# Revit family: 26891XXX_NEW
name_source: partatom
category: Plumbing Fixtures
revit_build: Autodesk Revit 2018 (Build: 20170223_1515(x64)
units: mm (PartAtom-declared; Revit-internal decimal feet)

## family parameters
Always vertical = No
Cut with Voids When Loaded = No
OmniClass Number = 23.45.00.00
OmniClass Title = Sanitary, Laundry, and Cleaning Equipment
Part Type = Normal
Room Calculation Point = No
Round Connector Dimension = Use Diameter
Shared = No
Work Plane-Based = Yes

## types (5) — shared parameters
Always visible = Yes
BIMobject category = Showers
Default Elevation = 1219.2 mm  [stored 4 ft]
Design country = Germany
EAN code = 4059625266021
Edition number = 1
GTIN code = https://4059625266021
IFC Classification = Sanitary Terminal
Installation instructions = https://www.hansgrohe.com
Manufacturer country = Germany
Manufacturer name = hansgrohe
Material main = Brass
Product Guid = 11db90c0-00a3-453a-81a2-86f946c703fb
Product SKU = 26891XXX
Product data url = https://www.bimobject.com
Product family = Croma Select S
Product group = Showerpipes with thermostat
Product name = 26891XXX Croma Select S Showerpipe 280 1jet EcoSmart 9 l/min with thermostat and hand shower Raindance Select S 120 3jet
Product url = https://www.hansgrohe.com
QR code = https://www.bimobject.com
Technical description = https://www.hansgrohe.com

## per-type parameters (varying)
| type | Material 1 |
| 990 Polished Gold Optic | Hansgrohe - Croma Select S - 990 Polished Gold Optic |
| 700 Matt White | Hansgrohe - Croma Select S - 700 Matt White |
| 670 Matte Black | Hansgrohe - Croma Select S - 670 Matte Black |
| 340 Brushed Black Chrome | Hansgrohe - Croma Select S - 340 Brushed Black Chrome |
| 140 Brushed Bronze | Hansgrohe - Croma Select S - 140 Brushed Bronze |

note: [stored X ft] marks values corroborated as IEEE doubles in the binary element streams (Revit-internal decimal feet)

## geometry (parser evidence)
native form markers: Sweep x3
no freeform markers — native parametric forms only
